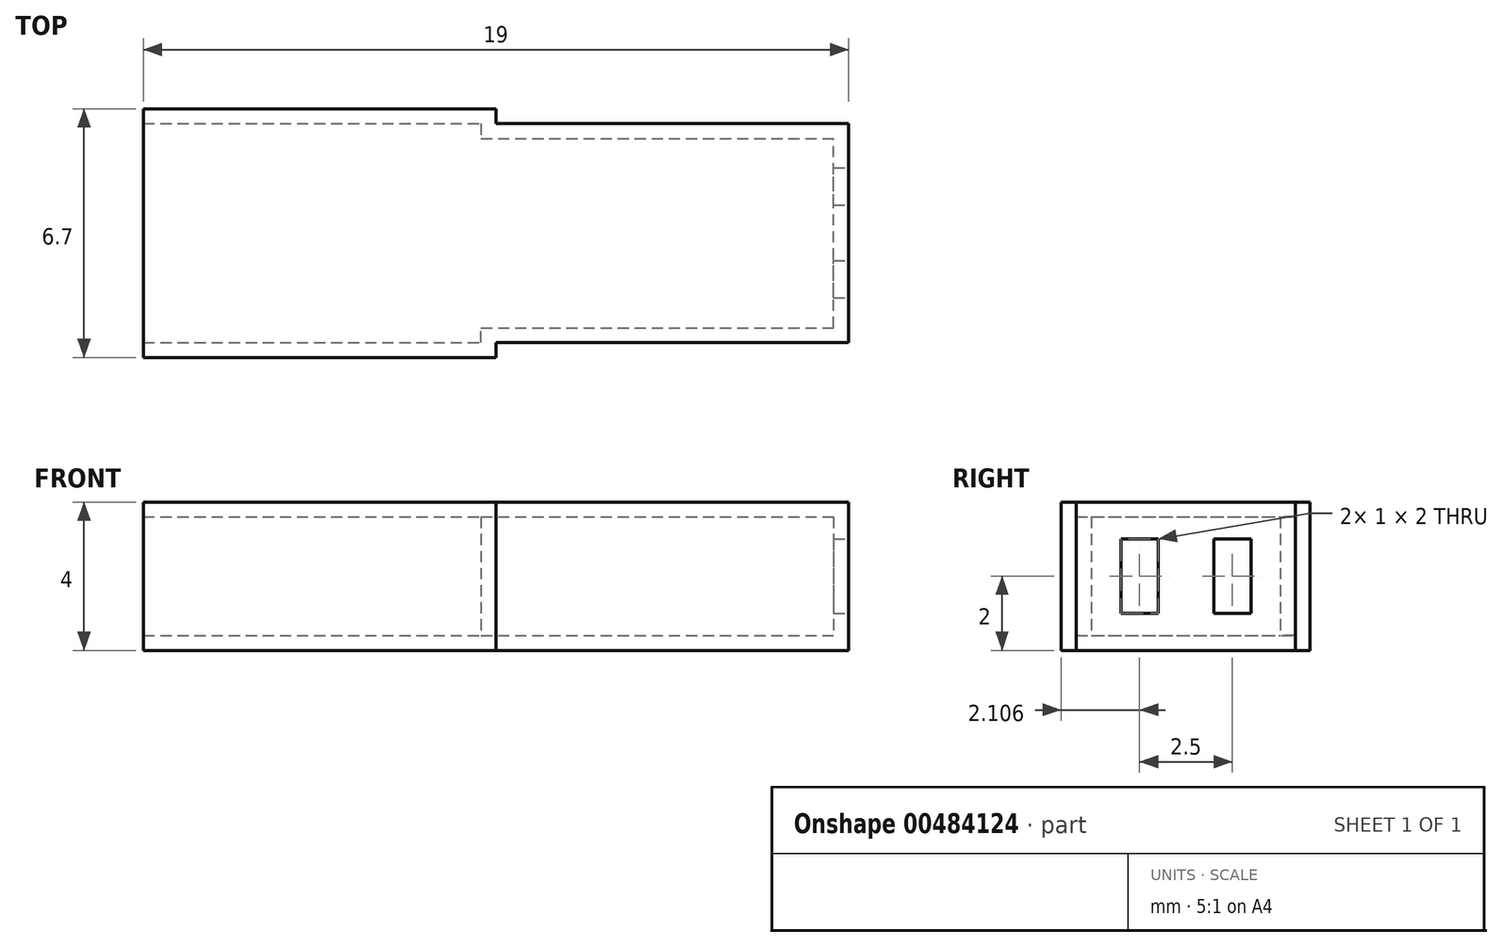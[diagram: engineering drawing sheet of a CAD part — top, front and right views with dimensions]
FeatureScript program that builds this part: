
annotation { "Feature Type Name" : "Feature", "Feature Type Description" : "" }
export const myFeature = defineFeature(function(context is Context, id is Id, definition is map)
    precondition{}
    {
        {
            var Q0;
            Q0=qCreatedBy(makeId("Top.planeOp"),FACE);
            var sketch = newSketch(context, id + "F0", { "sketchPlane" : qUnion([Q0])});
            skLineSegment(sketch, "E0", {"start": v(0, 0) * mm, "end": v(19, 0) * mm, "construction": true});
            skLineSegment(sketch, "E1", {"start": v(0, -3.35) * mm, "end": v(0, 3.35) * mm});
            skLineSegment(sketch, "E2", {"start": v(0, -3.35) * mm, "end": v(9.5, -3.35) * mm});
            skLineSegment(sketch, "E3", {"start": v(9.5, -3.35) * mm, "end": v(9.5, -2.95) * mm});
            skLineSegment(sketch, "E4", {"start": v(9.5, -2.95) * mm, "end": v(19, -2.95) * mm});
            skLineSegment(sketch, "E5", {"start": v(19, -2.95) * mm, "end": v(19, 2.95) * mm});
            skLineSegment(sketch, "E6", {"start": v(0, 3.35) * mm, "end": v(9.5, 3.35) * mm});
            skLineSegment(sketch, "E7", {"start": v(9.5, 3.35) * mm, "end": v(9.5, 2.95) * mm});
            skLineSegment(sketch, "E8", {"start": v(9.5, 2.95) * mm, "end": v(19, 2.95) * mm});
            skSolve(sketch);
        }
        {
            var Q0;
            Q0=makeQuery(id+"F0.imprint","IMPRINT",FACE,{"disambiguationData":[TD([[makeQuery(id+"F0.imprint","IMPRINT",EDGE,{"derivedFrom":sQuery(id+"F0.wireOp",EDGE,"E1")}),-1.0]])]});
            extrude(context, id + "F1", {"entities" : qUnion([Q0]), "depth" : 4 * mm});
        }
        {
            var Q0;
            Q0=makeQuery(id+"F1.opExtrude","SWEPT_FACE",FACE,{"disambiguationData":[OSD([sQuery(id+"F0.wireOp",EDGE,"E1")])]});
            shell(context, id + "F2", {"entities" : qUnion([Q0]), "thickness" : 0.4 * mm});
        }
        {
            var Q0;
            Q0=makeQuery(id+"F1.opExtrude","SWEPT_FACE",FACE,{"disambiguationData":[OSD([sQuery(id+"F0.wireOp",EDGE,"E5")])]});
            var sketch = newSketch(context, id + "F3", { "sketchPlane" : qUnion([Q0])});
            skLineSegment(sketch, "E9", {"start": v(0, 0) * mm, "end": v(0, 4) * mm, "construction": true});
            skLineSegment(sketch, "E10.bottom", {"start": v(-1.74, 3) * mm, "end": v(-0.74, 3) * mm});
            skLineSegment(sketch, "E10.top", {"start": v(-1.74, 1) * mm, "end": v(-0.74, 1) * mm});
            skLineSegment(sketch, "E10.left", {"start": v(-1.74, 3) * mm, "end": v(-1.74, 1) * mm});
            skLineSegment(sketch, "E10.right", {"start": v(-0.74, 3) * mm, "end": v(-0.74, 1) * mm});
            skLineSegment(sketch, "E11.bottom", {"start": v(0.76, 3) * mm, "end": v(1.76, 3) * mm});
            skLineSegment(sketch, "E11.top", {"start": v(0.76, 1) * mm, "end": v(1.76, 1) * mm});
            skLineSegment(sketch, "E11.left", {"start": v(0.76, 3) * mm, "end": v(0.76, 1) * mm});
            skLineSegment(sketch, "E11.right", {"start": v(1.76, 3) * mm, "end": v(1.76, 1) * mm});
            skLineSegment(sketch, "E12", {"start": v(0, 2) * mm, "end": v(-0.74, 2) * mm, "construction": true});
            skSolve(sketch);
        }
        {
            var Q0;
            Q0=makeQuery(id+"F3.imprint","IMPRINT",FACE,{"disambiguationData":[TD([[makeQuery(id+"F3.imprint","IMPRINT",EDGE,{"derivedFrom":sQuery(id+"F3.wireOp",EDGE,"E10.bottom")}),-1.0]])]});
            var Q1;
            Q1=makeQuery(id+"F3.imprint","IMPRINT",FACE,{"disambiguationData":[TD([[makeQuery(id+"F3.imprint","IMPRINT",EDGE,{"derivedFrom":sQuery(id+"F3.wireOp",EDGE,"E11.bottom")}),-1.0]])]});
            var Q2;
            Q2=makeQuery(id+"F2.opShell","OFFSET_FACE",FACE,{"disambiguationData":[OSD([sQuery(id+"F0.wireOp",EDGE,"E5")])]});
            extrude(context, id + "F4", {"entities" : qUnion([Q0, Q1]), "operationType" : NewBodyOperationType.REMOVE, "endBound" : BoundingType.UP_TO_SURFACE, "oppositeDirection" : true, "endBoundEntityFace" : qUnion([Q2]), "depth" : 25 * mm});
        }
    });
